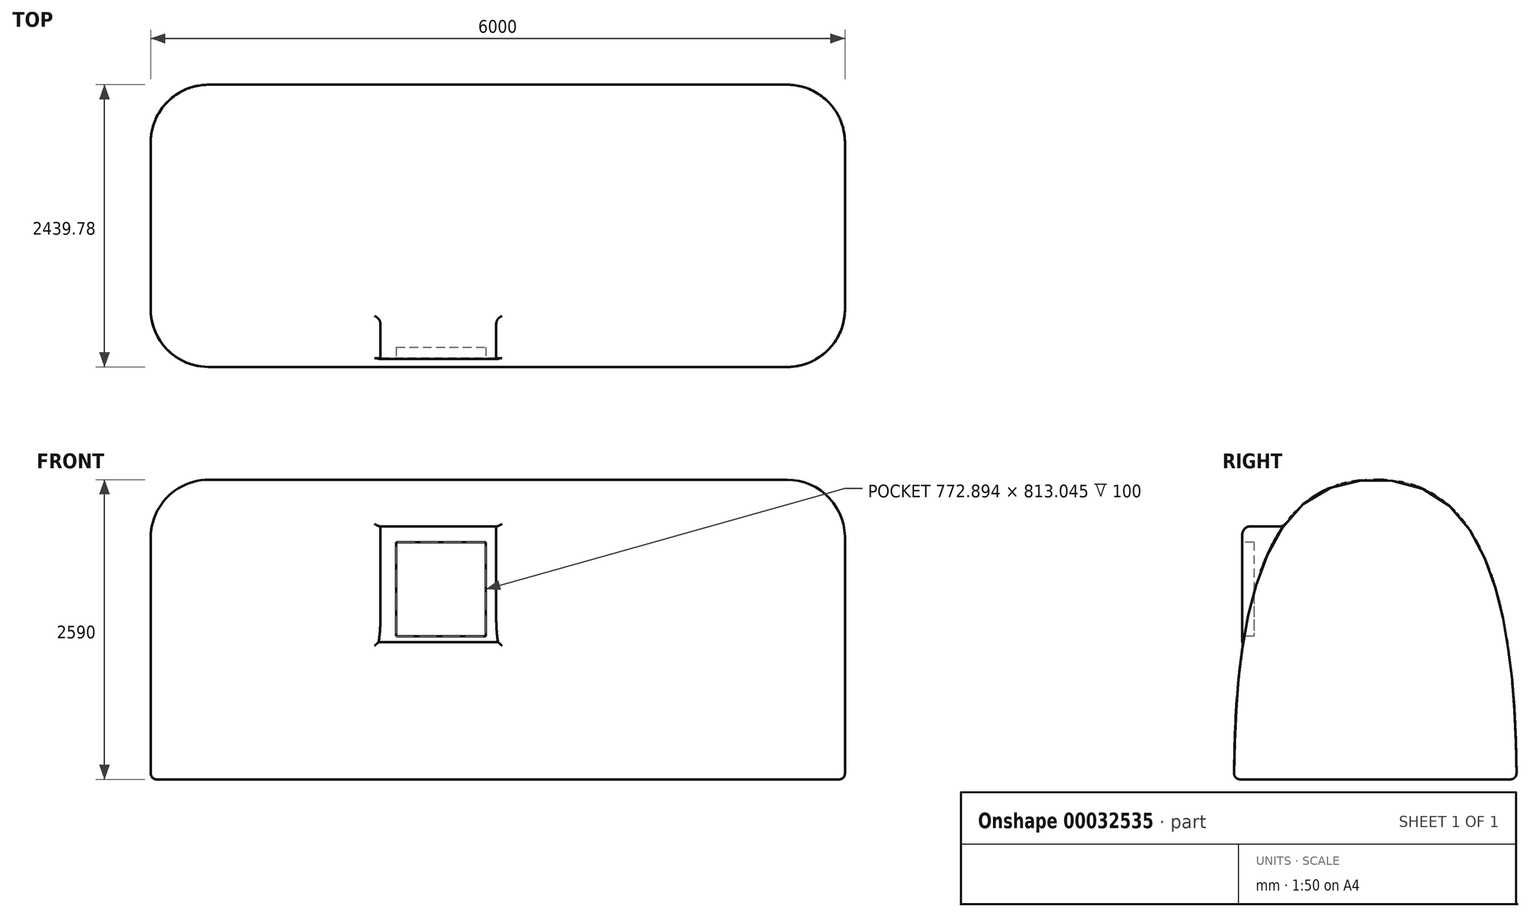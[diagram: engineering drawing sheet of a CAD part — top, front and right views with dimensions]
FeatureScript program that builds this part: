
annotation { "Feature Type Name" : "Feature", "Feature Type Description" : "" }
export const myFeature = defineFeature(function(context is Context, id is Id, definition is map)
    precondition{}
    {
        {
            var Q0;
            Q0=qCreatedBy(makeId("Right.planeOp"),FACE);
            var sketch = newSketch(context, id + "F0", { "sketchPlane" : qUnion([Q0])});
            skLineSegment(sketch, "E0", {"start": v(0, 0) * mm, "end": v(0, 2590) * mm, "construction": true});
            skLineSegment(sketch, "E1", {"start": v(0, 0) * mm, "end": v(-1220, 0) * mm});
            skLineSegment(sketch, "E2", {"start": v(0, 0) * mm, "end": v(1220, 0) * mm});
            skFitSpline(sketch, "E3", {"points": [v(-1220, 0) * mm, v(0, 2590) * mm, v(1220, 0) * mm], "startDerivative": vector(0, 13200) * mm, "endDerivative": vector(0, -13200) * mm});
            skLineSegment(sketch, "E4", {"start": v(-1220, 2200) * mm, "end": v(0, 2200) * mm, "construction": true});
            skLineSegment(sketch, "E5", {"start": v(0, 2200) * mm, "end": v(1220, 2200) * mm, "construction": true});
            skLineSegment(sketch, "E6", {"start": v(1220, 0) * mm, "end": v(1220, -965) * mm, "construction": true});
            skSolve(sketch);
        }
        {
            var Q0;
            Q0=makeQuery(id+"F0.imprint","IMPRINT",FACE,{"disambiguationData":[TD([[makeQuery(id+"F0.imprint","IMPRINT",EDGE,{"derivedFrom":sQuery(id+"F0.wireOp",EDGE,"E1")}),-1.0]])]});
            extrude(context, id + "F1", {"entities" : qUnion([Q0]), "depth" : 6000 * mm});
        }
        {
            var Q0;
            Q0=makeQuery(id+"F1.opExtrude","CAP_EDGE",EDGE,{"disambiguationData":[OSD([sQuery(id+"F0.wireOp",EDGE,"E3")])],"isStart":false});
            var Q1;
            Q1=makeQuery(id+"F1.opExtrude","CAP_EDGE",EDGE,{"disambiguationData":[OSD([sQuery(id+"F0.wireOp",EDGE,"E3")])],"isStart":true});
            fillet(context, id + "F2", {"entities" : qUnion([Q0, Q1]), "radius" : 500 * mm, "tangentPropagation" : true, "allowEdgeOverflow" : false});
        }
        {
            var Q0;
            Q0=makeQuery(id+"F1.opExtrude","SWEPT_FACE",FACE,{"disambiguationData":[OSD([sQuery(id+"F0.wireOp",EDGE,"E1"),sQuery(id+"F0.wireOp",EDGE,"E2")])]});
            fillet(context, id + "F3", {"entities" : qUnion([Q0]), "radius" : 50 * mm, "tangentPropagation" : true, "allowEdgeOverflow" : false});
        }
        {
            var Q0;
            Q0=qCreatedBy(makeId("Front.planeOp"),FACE);
            var sketch = newSketch(context, id + "F4", { "sketchPlane" : qUnion([Q0])});
            skLineSegment(sketch, "E7.bottom", {"start": v(1985.5, 2187.39) * mm, "end": v(2985.86, 2187.39) * mm});
            skLineSegment(sketch, "E7.top", {"start": v(1985.5, 1186.9) * mm, "end": v(2985.86, 1186.9) * mm});
            skLineSegment(sketch, "E7.left", {"start": v(1985.5, 2187.39) * mm, "end": v(1985.5, 1186.9) * mm});
            skLineSegment(sketch, "E7.right", {"start": v(2985.86, 2187.39) * mm, "end": v(2985.86, 1186.9) * mm});
            skSolve(sketch);
        }
        {
            var Q0;
            Q0 = qSketchRegion(id + "F4", true);
            var Q1;
            Q1=makeQuery(id+"F1.opExtrude","SWEPT_FACE",FACE,{"disambiguationData":[OSD([sQuery(id+"F0.wireOp",EDGE,"E3")])]});
            extrude(context, id + "F5", {"entities" : qUnion([Q0]), "operationType" : NewBodyOperationType.ADD, "endBoundEntityFace" : qUnion([Q1]), "depth" : 1150 * mm});
        }
        {
            var Q0;
            Q0=makeQuery(id+"F5.boolean.opBoolean","INTERSECT",EDGE,{"derivedFrom":[makeQuery(id+"F1.opExtrude","SWEPT_FACE",FACE,{"disambiguationData":[OSD([sQuery(id+"F0.wireOp",EDGE,"E3")])]}),makeQuery(id+"F5.opExtrude","SWEPT_FACE",FACE,{"disambiguationData":[OSD([sQuery(id+"F4.wireOp",EDGE,"E7.bottom")])]})]});
            var Q1;
            Q1=makeQuery(id+"F5.boolean.opBoolean","INTERSECT",EDGE,{"derivedFrom":[makeQuery(id+"F1.opExtrude","SWEPT_FACE",FACE,{"disambiguationData":[OSD([sQuery(id+"F0.wireOp",EDGE,"E3")])]}),makeQuery(id+"F5.opExtrude","SWEPT_FACE",FACE,{"disambiguationData":[OSD([sQuery(id+"F4.wireOp",EDGE,"E7.right")])]})]});
            var Q2;
            Q2=makeQuery(id+"F5.boolean.opBoolean","INTERSECT",EDGE,{"derivedFrom":[makeQuery(id+"F1.opExtrude","SWEPT_FACE",FACE,{"disambiguationData":[OSD([sQuery(id+"F0.wireOp",EDGE,"E3")])]}),makeQuery(id+"F5.opExtrude","SWEPT_FACE",FACE,{"disambiguationData":[OSD([sQuery(id+"F4.wireOp",EDGE,"E7.top")])]})]});
            var Q3;
            Q3=makeQuery(id+"F5.boolean.opBoolean","INTERSECT",EDGE,{"derivedFrom":[makeQuery(id+"F1.opExtrude","SWEPT_FACE",FACE,{"disambiguationData":[OSD([sQuery(id+"F0.wireOp",EDGE,"E3")])]}),makeQuery(id+"F5.opExtrude","SWEPT_FACE",FACE,{"disambiguationData":[OSD([sQuery(id+"F4.wireOp",EDGE,"E7.left")])]})]});
            fillet(context, id + "F6", {"entities" : qUnion([Q0, Q1, Q2, Q3]), "radius" : 50 * mm, "tangentPropagation" : true, "rho" : .5, "crossSection" : FilletCrossSection.CONIC, "allowEdgeOverflow" : false});
        }
        {
            var Q0;
            Q0=makeQuery(id+"F5.opExtrude","CAP_EDGE",EDGE,{"disambiguationData":[OSD([sQuery(id+"F4.wireOp",EDGE,"E7.bottom")])],"isStart":false});
            fillet(context, id + "F7", {"entities" : qUnion([Q0]), "radius" : 72.43 * mm, "tangentPropagation" : true, "allowEdgeOverflow" : false});
        }
        {
            var Q0;
            Q0=makeQuery(id+"F5.opExtrude","CAP_FACE",FACE,{"disambiguationData":[OSD([sQuery(id+"F4.wireOp",EDGE,"E7.bottom"),sQuery(id+"F4.wireOp",EDGE,"E7.top"),sQuery(id+"F4.wireOp",EDGE,"E7.left"),sQuery(id+"F4.wireOp",EDGE,"E7.right")])],"isStart":false});
            var sketch = newSketch(context, id + "F8", { "sketchPlane" : qUnion([Q0])});
            skLineSegment(sketch, "E8.bottom", {"start": v(2122.22, 2051.22) * mm, "end": v(2895.12, 2051.22) * mm});
            skLineSegment(sketch, "E8.top", {"start": v(2122.22, 1238.18) * mm, "end": v(2895.12, 1238.18) * mm});
            skLineSegment(sketch, "E8.left", {"start": v(2122.22, 2051.22) * mm, "end": v(2122.22, 1238.18) * mm});
            skLineSegment(sketch, "E8.right", {"start": v(2895.12, 2051.22) * mm, "end": v(2895.12, 1238.18) * mm});
            skSolve(sketch);
        }
        {
            var Q0;
            Q0=makeQuery(id+"F8.imprint","IMPRINT",FACE,{"disambiguationData":[TD([[makeQuery(id+"F8.imprint","IMPRINT",EDGE,{"derivedFrom":sQuery(id+"F8.wireOp",EDGE,"E8.bottom")}),-1.0]])]});
            extrude(context, id + "F9", {"entities" : qUnion([Q0]), "operationType" : NewBodyOperationType.REMOVE, "oppositeDirection" : true, "depth" : 100 * mm});
        }
    });
